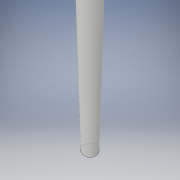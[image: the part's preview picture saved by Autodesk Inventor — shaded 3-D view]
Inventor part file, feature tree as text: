
AUTODESK INVENTOR PART (.ipt)
format: ipt  version: 2019 (Build 230136000, 136)  size: 90,624 bytes
history: native  units: in
note: dims shown in document units (in); Inventor stores cm internally (conversion verified against a paired STEP export)
features: extrude x1, sketch x1
ambient origin geometry x8: Origin, YZ Plane, XZ Plane, XY Plane, X Axis, Y Axis, Z Axis, Center Point
bodies: Solid1 (feature_tree)
feature tree (2):
  extrude  "Extrusion1"  Depth=3.0in TaperAngle=0.0deg
  sketch  "Sketch1"  dims[d0=0.375in d1=3.0in d2=0.0in]
